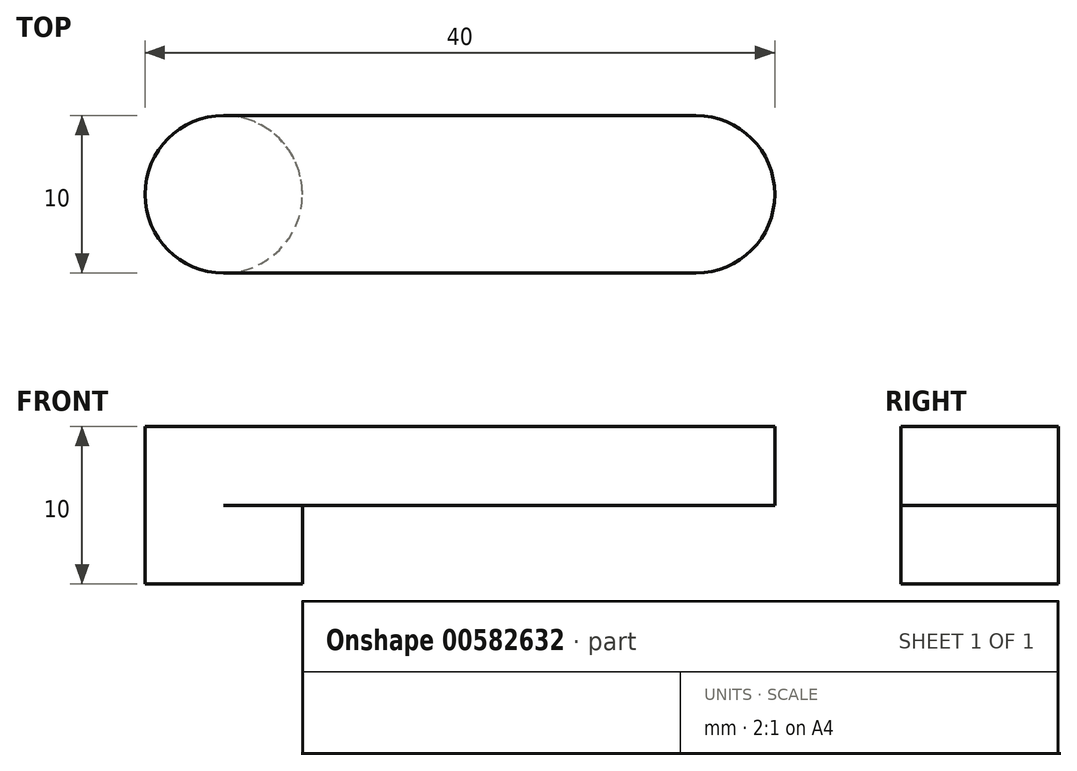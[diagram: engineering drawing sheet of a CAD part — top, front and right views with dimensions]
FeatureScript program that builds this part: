
annotation { "Feature Type Name" : "Feature", "Feature Type Description" : "" }
export const myFeature = defineFeature(function(context is Context, id is Id, definition is map)
    precondition{}
    {
        {
            var Q0;
            Q0=qCreatedBy(makeId("Top.planeOp"),FACE);
            var sketch = newSketch(context, id + "F0", { "sketchPlane" : qUnion([Q0])});
            skCircle(sketch, "E0", {"center": v(0, 0) * mm, "radius": 5 * mm});
            skSolve(sketch);
        }
        {
            var Q0;
            Q0=qCreatedBy(makeId("Top.planeOp"),FACE);
            var sketch = newSketch(context, id + "F1", { "sketchPlane" : qUnion([Q0])});
            skLineSegment(sketch, "E1", {"start": v(0, 5) * mm, "end": v(30, 5) * mm});
            skLineSegment(sketch, "E2", {"start": v(0, -5) * mm, "end": v(30, -5) * mm});
            skArc(sketch, "E3", {"start": v(30, -5) * mm, "mid": v(35, 0) * mm, "end": v(30, 5) * mm});
            skArc(sketch, "E4", {"start": v(0, -5) * mm, "mid": v(5, 0) * mm, "end": v(0, 5) * mm});
            skSolve(sketch);
        }
        {
            var Q0;
            Q0=makeQuery(id+"F0.imprint","IMPRINT",FACE,{"disambiguationData":[TD([[makeQuery(id+"F0.imprint","IMPRINT",EDGE,{"derivedFrom":sQuery(id+"F0.wireOp",EDGE,"E0")}),1.0]])]});
            var Q1;
            Q1=makeQuery(id+"F1.imprint","IMPRINT",FACE,{"disambiguationData":[TD([[makeQuery(id+"F1.imprint","IMPRINT",EDGE,{"derivedFrom":sQuery(id+"F1.wireOp",EDGE,"E1")}),-1.0]])]});
            extrude(context, id + "F2", {"entities" : qUnion([Q0, Q1]), "depth" : 5 * mm, "offsetDistance" : 25 * mm});
        }
        {
            var Q0;
            Q0=makeQuery(id+"F2.opExtrude","CAP_FACE",FACE,{"disambiguationData":[OSD([sQuery(id+"F0.wireOp",EDGE,"E0")])],"isStart":true});
            extrude(context, id + "F3", {"entities" : qUnion([Q0]), "operationType" : NewBodyOperationType.ADD, "depth" : 5 * mm, "offsetDistance" : 25 * mm});
        }
    });
